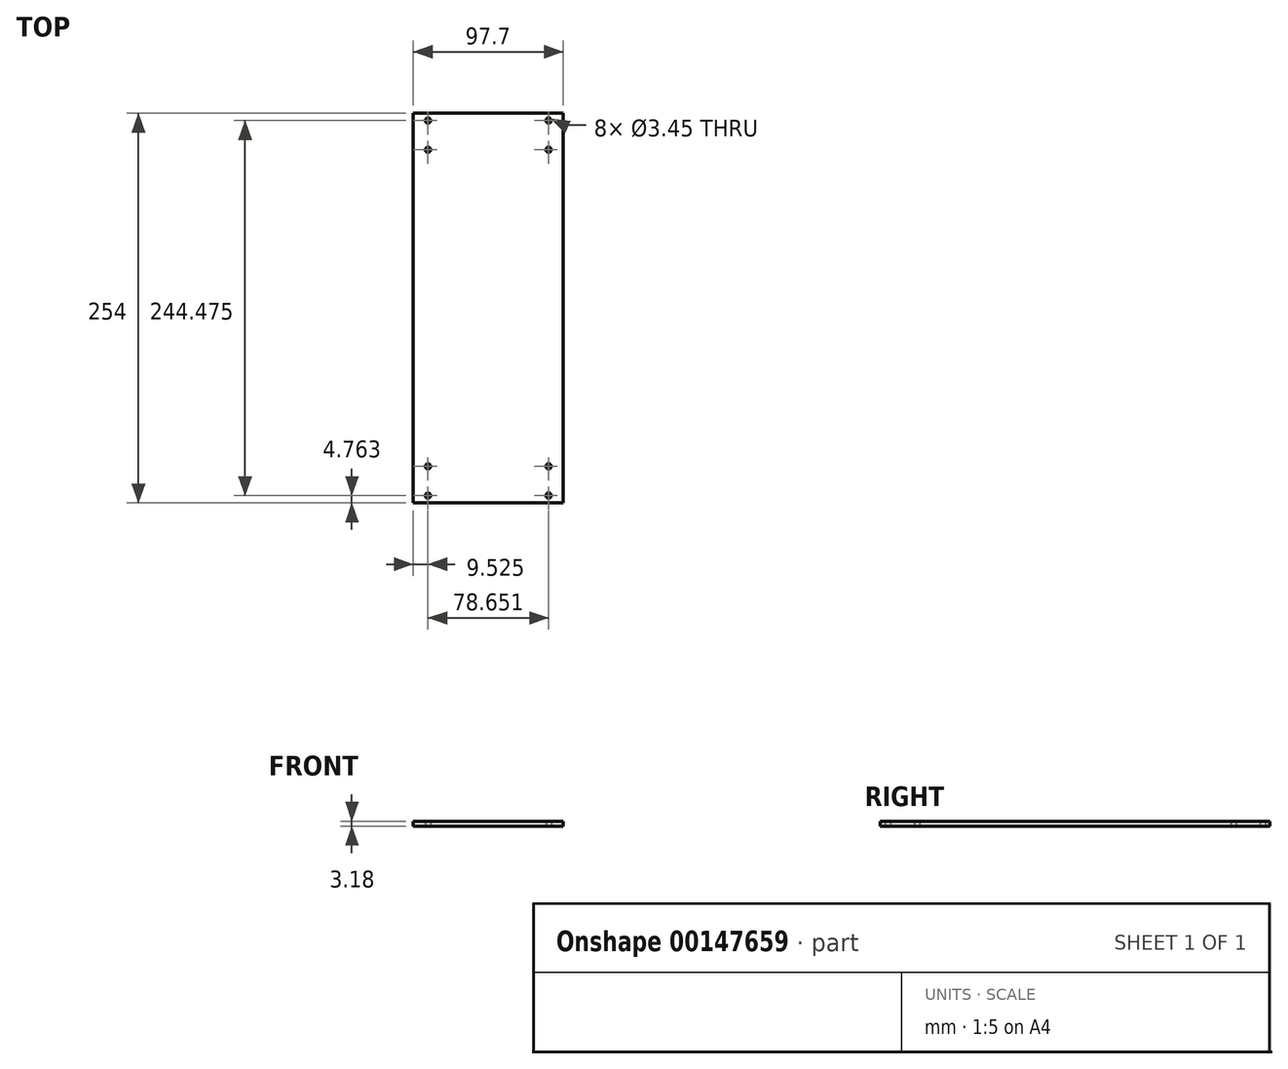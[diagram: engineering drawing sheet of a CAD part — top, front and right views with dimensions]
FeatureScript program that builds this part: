
annotation { "Feature Type Name" : "Feature", "Feature Type Description" : "" }
export const myFeature = defineFeature(function(context is Context, id is Id, definition is map)
    precondition{}
    {
        {
            var Q0;
            Q0=qCreatedBy(makeId("Top.planeOp"),FACE);
            var sketch = newSketch(context, id + "F0", { "sketchPlane" : qUnion([Q0])});
            skLineSegment(sketch, "E0.bottom", {"start": v(48.85, -127) * mm, "end": v(-48.85, -127) * mm});
            skLineSegment(sketch, "E0.top", {"start": v(48.85, 127) * mm, "end": v(-48.85, 127) * mm});
            skLineSegment(sketch, "E0.left", {"start": v(48.85, -127) * mm, "end": v(48.85, 127) * mm});
            skLineSegment(sketch, "E0.right", {"start": v(-48.85, -127) * mm, "end": v(-48.85, 127) * mm});
            skPoint(sketch, "E0.middle", {"position": v(0, 0) * mm});
            skLineSegment(sketch, "E1", {"start": v(39.33, 103.19) * mm, "end": v(48.85, 103.19) * mm, "construction": true});
            skLineSegment(sketch, "E2.bottom", {"start": v(39.33, 103.19) * mm, "end": v(-39.33, 103.19) * mm, "construction": true});
            skLineSegment(sketch, "E2.top", {"start": v(39.33, -103.19) * mm, "end": v(-39.33, -103.19) * mm, "construction": true});
            skLineSegment(sketch, "E2.left", {"start": v(39.33, 103.19) * mm, "end": v(39.33, -103.19) * mm, "construction": true});
            skLineSegment(sketch, "E2.right", {"start": v(-39.33, 103.19) * mm, "end": v(-39.33, -103.19) * mm, "construction": true});
            skCircle(sketch, "E3", {"center": v(39.33, 103.19) * mm, "radius": 1.73 * mm});
            skCircle(sketch, "E4", {"center": v(-39.33, -103.19) * mm, "radius": 1.73 * mm});
            skLineSegment(sketch, "E5", {"start": v(0, 103.19) * mm, "end": v(0, 127) * mm, "construction": true});
            skLineSegment(sketch, "E6", {"start": v(39.33, 103.19) * mm, "end": v(39.33, 122.24) * mm, "construction": true});
            skCircle(sketch, "E7", {"center": v(-39.33, 103.19) * mm, "radius": 1.73 * mm});
            skCircle(sketch, "E8", {"center": v(39.33, -103.19) * mm, "radius": 1.73 * mm});
            skLineSegment(sketch, "E9", {"start": v(39.33, 122.24) * mm, "end": v(39.33, 127) * mm, "construction": true});
            skCircle(sketch, "E10", {"center": v(39.33, 122.24) * mm, "radius": 1.73 * mm});
            skLineSegment(sketch, "E11", {"start": v(-39.33, 103.19) * mm, "end": v(-39.33, 122.24) * mm, "construction": true});
            skLineSegment(sketch, "E12", {"start": v(-39.33, 122.24) * mm, "end": v(-39.33, 127) * mm, "construction": true});
            skLineSegment(sketch, "E13", {"start": v(-39.33, -103.19) * mm, "end": v(-39.33, -122.24) * mm, "construction": true});
            skLineSegment(sketch, "E14", {"start": v(-39.33, -122.24) * mm, "end": v(-39.33, -127) * mm, "construction": true});
            skLineSegment(sketch, "E15", {"start": v(39.33, -103.19) * mm, "end": v(39.33, -122.24) * mm, "construction": true});
            skLineSegment(sketch, "E16", {"start": v(39.33, -122.24) * mm, "end": v(39.33, -127) * mm, "construction": true});
            skCircle(sketch, "E17", {"center": v(-39.33, 122.24) * mm, "radius": 1.73 * mm});
            skCircle(sketch, "E18", {"center": v(-39.33, -122.24) * mm, "radius": 1.73 * mm});
            skCircle(sketch, "E19", {"center": v(39.33, -122.24) * mm, "radius": 1.73 * mm});
            skSolve(sketch);
        }
        {
            var Q0;
            Q0=makeQuery(id+"F0.imprint","IMPRINT",FACE,{"disambiguationData":[TD([[makeQuery(id+"F0.imprint","IMPRINT",EDGE,{"derivedFrom":sQuery(id+"F0.wireOp",EDGE,"E0.bottom")}),-1.0]])]});
            extrude(context, id + "F1", {"entities" : qUnion([Q0]), "depth" : 3.17 * mm});
        }
    });
